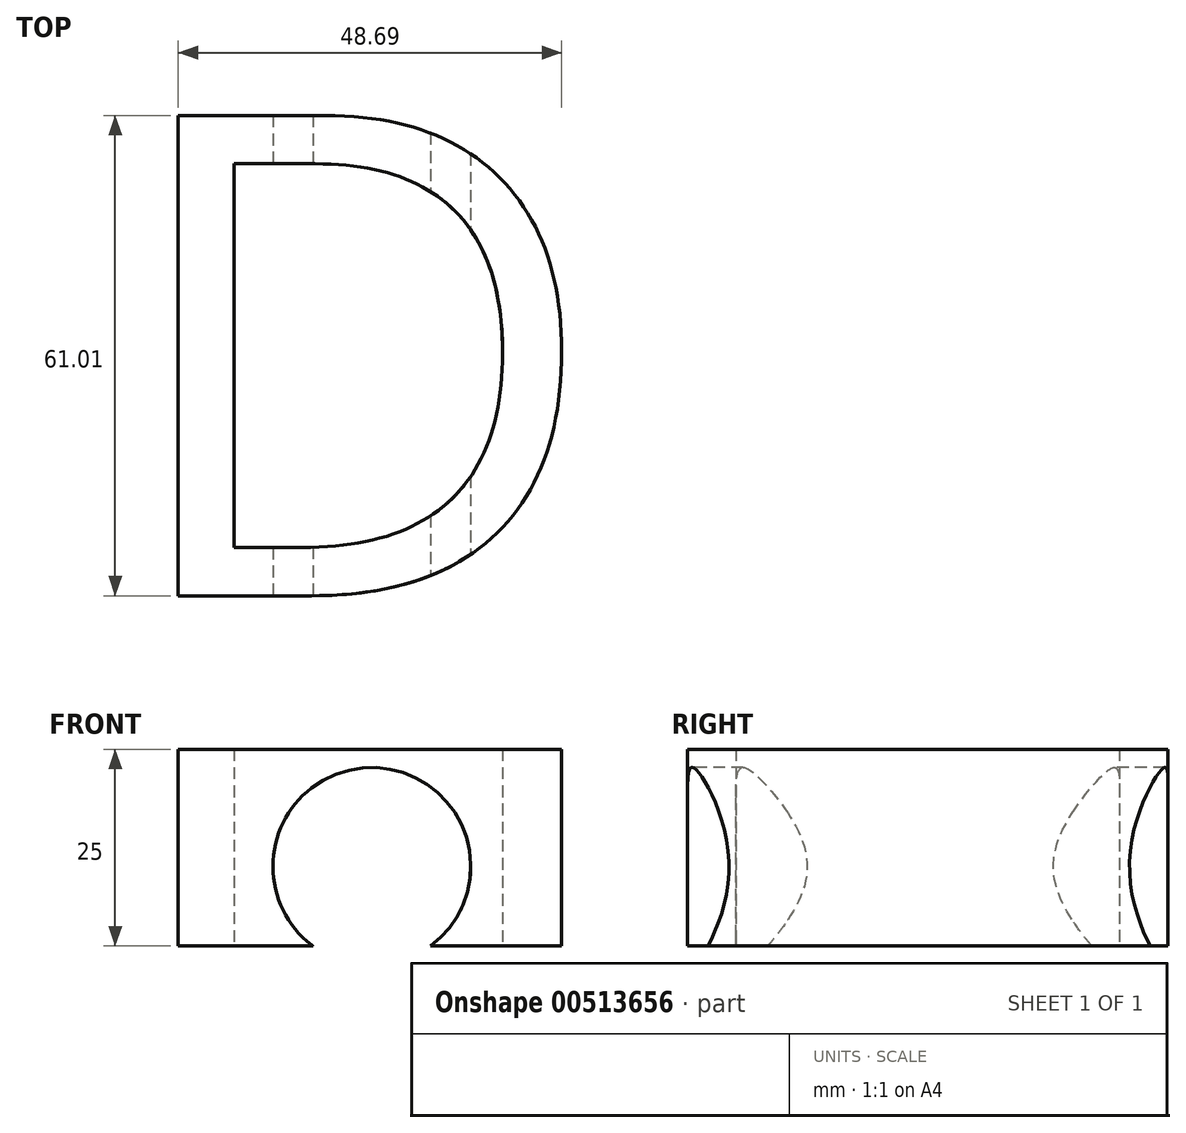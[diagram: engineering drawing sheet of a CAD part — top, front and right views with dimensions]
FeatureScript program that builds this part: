
annotation { "Feature Type Name" : "Feature", "Feature Type Description" : "" }
export const myFeature = defineFeature(function(context is Context, id is Id, definition is map)
    precondition{}
    {
        {
            var Q0;
            Q0=qCreatedBy(makeId("Top.planeOp"),FACE);
            var sketch = newSketch(context, id + "F0", { "sketchPlane" : qUnion([Q0])});
            skText(sketch, "E0", { "text": "D", "fontName": "OpenSans-Regular.ttf"});
            const initialGuessF0  = {"E0": [-0.02877, 0, 1, 0, 0.06153]};
            skSetInitialGuess(sketch, initialGuessF0);
            skSolve(sketch);
        }
        {
            var Q0;
            Q0 = qSketchRegion(id + "F0", true);
            extrude(context, id + "F1", {"entities" : qUnion([Q0]), "depth" : 25 * mm});
        }
        {
            var Q0;
            Q0=qCreatedBy(makeId("Front.planeOp"),FACE);
            var sketch = newSketch(context, id + "F2", { "sketchPlane" : qUnion([Q0])});
            skCircle(sketch, "E1", {"center": v(4.2, 10.1) * mm, "radius": 12.57 * mm});
            skSolve(sketch);
        }
        {
            var Q0;
            Q0 = qSketchRegion(id + "F2", true);
            extrude(context, id + "F3", {"entities" : qUnion([Q0]), "operationType" : NewBodyOperationType.REMOVE, "oppositeDirection" : true, "depth" : 84.05 * mm});
        }
    });
